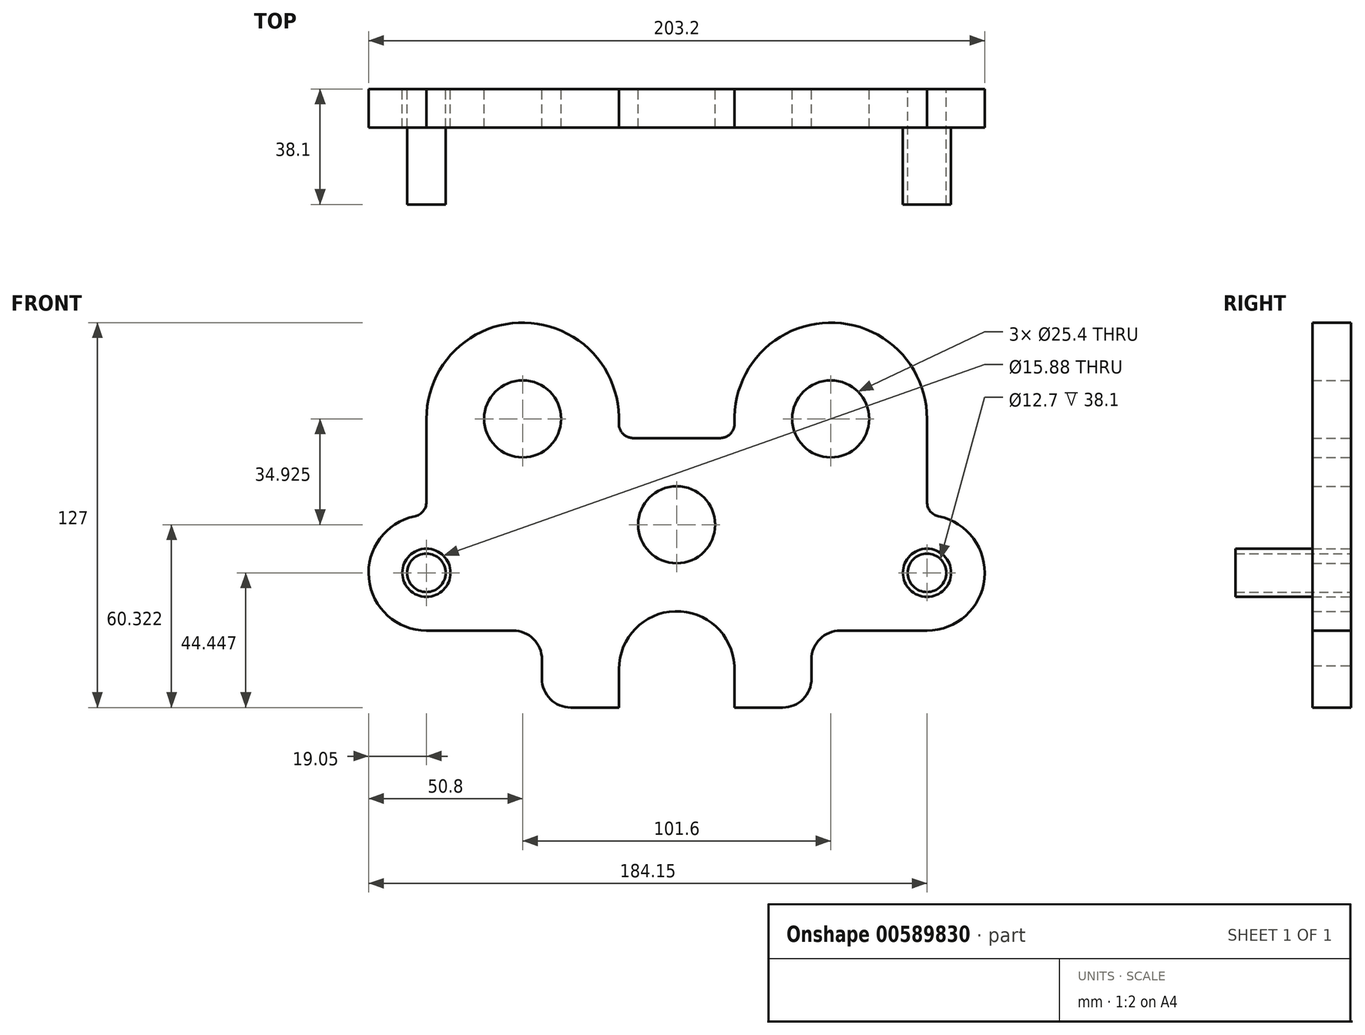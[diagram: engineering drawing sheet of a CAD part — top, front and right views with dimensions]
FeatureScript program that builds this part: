
annotation { "Feature Type Name" : "Feature", "Feature Type Description" : "" }
export const myFeature = defineFeature(function(context is Context, id is Id, definition is map)
    precondition{}
    {
        {
            var Q0;
            Q0=qCreatedBy(makeId("Front.planeOp"),FACE);
            var sketch = newSketch(context, id + "F0", { "sketchPlane" : qUnion([Q0])});
            skCircle(sketch, "E0", {"center": v(0, -42.39) * mm, "radius": 12.7 * mm});
            skCircle(sketch, "E1", {"center": v(50.8, -7.46) * mm, "radius": 12.7 * mm});
            skCircle(sketch, "E2", {"center": v(82.55, -58.26) * mm, "radius": 6.35 * mm});
            skCircle(sketch, "E3.MirrorC", {"center": v(-50.8, -7.46) * mm, "radius": 12.7 * mm});
            skCircle(sketch, "E4.MirrorC", {"center": v(-82.55, -58.26) * mm, "radius": 6.35 * mm});
            skArc(sketch, "E5", {"start": v(19.08, -8.84) * mm, "mid": v(50.1, 24.28) * mm, "end": v(82.55, -7.46) * mm});
            skArc(sketch, "E6", {"start": v(-19.08, -8.84) * mm, "mid": v(-50.1, 24.28) * mm, "end": v(-82.55, -7.46) * mm});
            skArc(sketch, "E7", {"start": v(-86.36, -39.6) * mm, "mid": v(-101.5, -60.18) * mm, "end": v(-82.55, -77.31) * mm});
            skArc(sketch, "E8", {"start": v(86.36, -39.6) * mm, "mid": v(101.5, -60.18) * mm, "end": v(82.55, -77.31) * mm});
            skLineSegment(sketch, "E9", {"start": v(82.55, -7.46) * mm, "end": v(82.55, -34.93) * mm});
            skLineSegment(sketch, "E10.MirrorCS", {"start": v(-82.55, -7.46) * mm, "end": v(-82.55, -34.93) * mm});
            skLineSegment(sketch, "E11", {"start": v(0, 87.14) * mm, "end": v(0, -112.55) * mm, "construction": true});
            skLineSegment(sketch, "E12", {"start": v(-82.55, -77.31) * mm, "end": v(-53.97, -77.31) * mm});
            skLineSegment(sketch, "E13", {"start": v(-44.45, -86.84) * mm, "end": v(-44.45, -93.19) * mm});
            skLineSegment(sketch, "E14", {"start": v(-34.92, -102.71) * mm, "end": v(-19.03, -102.71) * mm});
            skLineSegment(sketch, "E15.MirrorCS", {"start": v(82.55, -77.31) * mm, "end": v(53.98, -77.31) * mm});
            skLineSegment(sketch, "E16.MirrorCS", {"start": v(44.45, -86.84) * mm, "end": v(44.45, -93.19) * mm});
            skLineSegment(sketch, "E17.MirrorCS", {"start": v(34.93, -102.71) * mm, "end": v(19.03, -102.71) * mm});
            skLineSegment(sketch, "E18", {"start": v(-19.03, -102.71) * mm, "end": v(-19.03, -90.01) * mm});
            skArc(sketch, "E19", {"start": v(-19.03, -90.01) * mm, "mid": v(-0.52, -70.97) * mm, "end": v(19.04, -88.94) * mm});
            skLineSegment(sketch, "E20", {"start": v(19.03, -102.71) * mm, "end": v(19.04, -88.94) * mm});
            skPoint(sketch, "E21.visualSharp", {"position": v(-82.55, -39.21) * mm});
            skArc(sketch, "E21.filletArc", {"start": v(-86.36, -39.6) * mm, "mid": v(-83.62, -37.94) * mm, "end": v(-82.55, -34.93) * mm});
            skPoint(sketch, "E22.visualSharp", {"position": v(-44.45, -77.31) * mm});
            skArc(sketch, "E22.filletArc", {"start": v(-44.45, -86.84) * mm, "mid": v(-47.24, -80.1) * mm, "end": v(-53.97, -77.31) * mm});
            skPoint(sketch, "E23.visualSharp", {"position": v(-44.45, -102.71) * mm});
            skArc(sketch, "E23.filletArc", {"start": v(-44.45, -93.19) * mm, "mid": v(-41.66, -99.92) * mm, "end": v(-34.92, -102.71) * mm});
            skPoint(sketch, "E24.visualSharp", {"position": v(82.55, -39.21) * mm});
            skArc(sketch, "E24.filletArc", {"start": v(82.55, -34.93) * mm, "mid": v(83.62, -37.94) * mm, "end": v(86.36, -39.6) * mm});
            skPoint(sketch, "E25.visualSharp", {"position": v(44.45, -77.31) * mm});
            skArc(sketch, "E25.filletArc", {"start": v(53.98, -77.31) * mm, "mid": v(47.24, -80.1) * mm, "end": v(44.45, -86.84) * mm});
            skPoint(sketch, "E26.visualSharp", {"position": v(44.45, -102.71) * mm});
            skArc(sketch, "E26.filletArc", {"start": v(34.93, -102.71) * mm, "mid": v(41.66, -99.92) * mm, "end": v(44.45, -93.19) * mm});
            skLineSegment(sketch, "E27", {"start": v(-14.32, -13.81) * mm, "end": v(0, -13.81) * mm});
            skLineSegment(sketch, "E28.MirrorCS", {"start": v(14.32, -13.81) * mm, "end": v(0, -13.81) * mm});
            skPoint(sketch, "E29.visualSharp", {"position": v(-19.74, -13.81) * mm});
            skArc(sketch, "E29.filletArc", {"start": v(-19.08, -8.84) * mm, "mid": v(-17.76, -12.34) * mm, "end": v(-14.32, -13.81) * mm});
            skPoint(sketch, "E30.visualSharp", {"position": v(19.74, -13.81) * mm});
            skArc(sketch, "E30.filletArc", {"start": v(14.32, -13.81) * mm, "mid": v(17.76, -12.34) * mm, "end": v(19.08, -8.84) * mm});
            skCircle(sketch, "E31", {"center": v(-82.55, -58.26) * mm, "radius": 7.94 * mm});
            skCircle(sketch, "E32", {"center": v(82.55, -58.26) * mm, "radius": 7.94 * mm});
            skSolve(sketch);
        }
        {
            var Q0;
            Q0=makeQuery(id+"F0.imprint","IMPRINT",FACE,{"disambiguationData":[TD([[makeQuery(id+"F0.imprint","IMPRINT",EDGE,{"derivedFrom":sQuery(id+"F0.wireOp",EDGE,"E0")}),-1.0]])]});
            var Q1;
            Q1=makeQuery(id+"F0.imprint","IMPRINT",FACE,{"disambiguationData":[TD([[makeQuery(id+"F0.imprint","IMPRINT",EDGE,{"derivedFrom":sQuery(id+"F0.wireOp",EDGE,"E2")}),-1.0]])]});
            var Q2;
            Q2=makeQuery(id+"F0.imprint","IMPRINT",FACE,{"disambiguationData":[TD([[makeQuery(id+"F0.imprint","IMPRINT",EDGE,{"derivedFrom":sQuery(id+"F0.wireOp",EDGE,"E4.MirrorC")}),1.0]])]});
            extrude(context, id + "F1", {"entities" : qUnion([Q0, Q1, Q2]), "endBound" : BoundingType.SYMMETRIC, "depth" : 12.7 * mm, "offsetDistance" : 25.4 * mm});
        }
        {
            var Q0;
            Q0=makeQuery(id+"F0.imprint","IMPRINT",FACE,{"disambiguationData":[TD([[makeQuery(id+"F0.imprint","IMPRINT",EDGE,{"derivedFrom":sQuery(id+"F0.wireOp",EDGE,"E4.MirrorC")}),1.0]])]});
            var Q1;
            Q1=makeQuery(id+"F0.imprint","IMPRINT",FACE,{"disambiguationData":[TD([[makeQuery(id+"F0.imprint","IMPRINT",EDGE,{"derivedFrom":sQuery(id+"F0.wireOp",EDGE,"E2")}),-1.0]])]});
            extrude(context, id + "F2", {"entities" : qUnion([Q0, Q1]), "operationType" : NewBodyOperationType.ADD, "depth" : 31.75 * mm, "offsetDistance" : 25.4 * mm});
        }
    });
